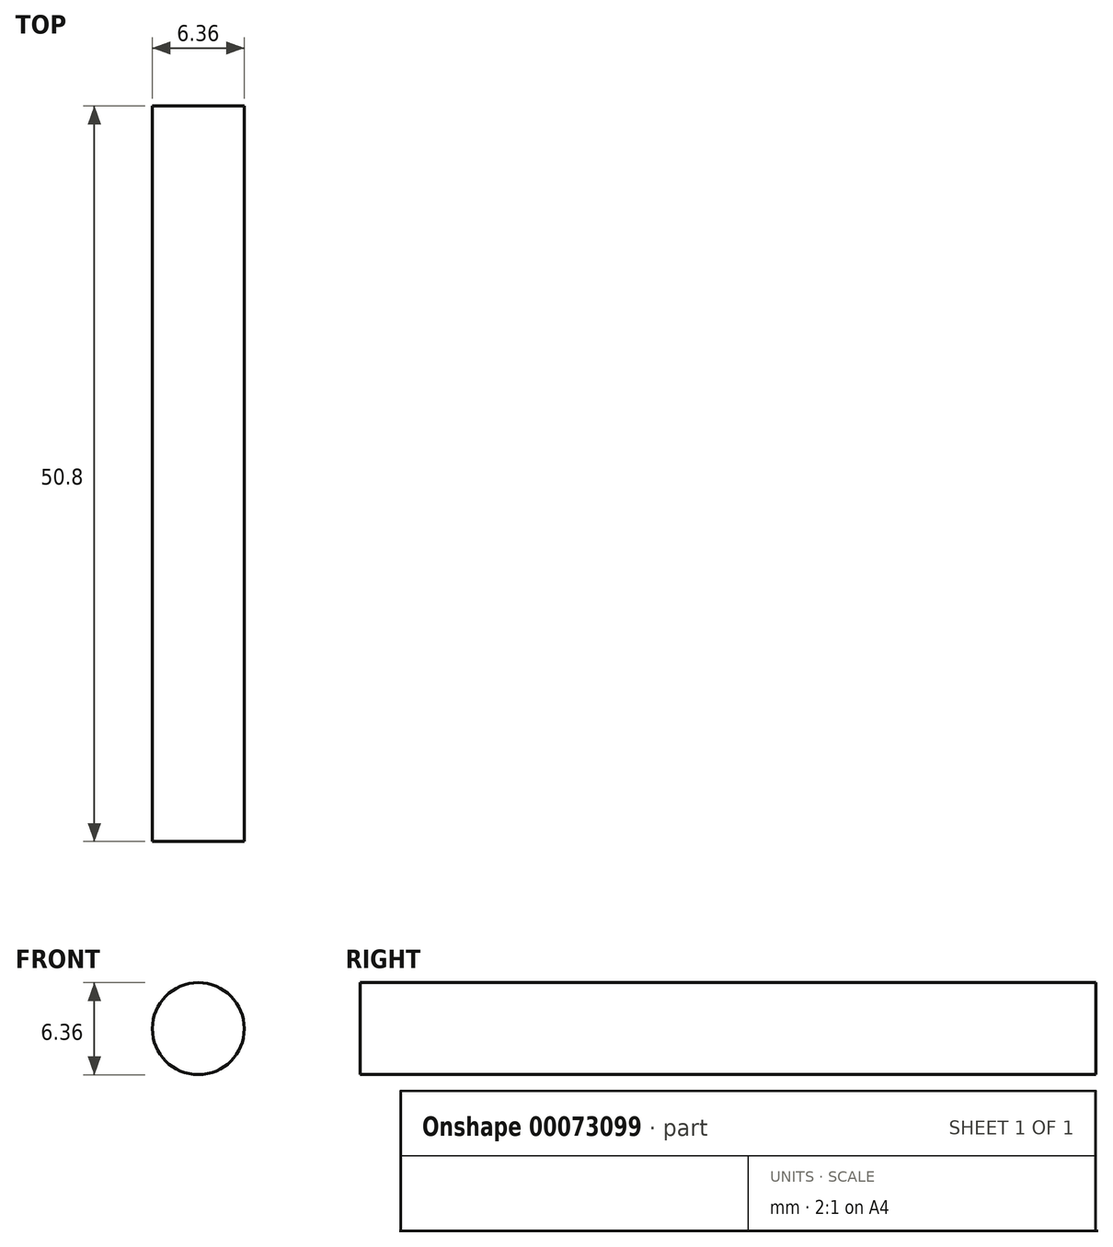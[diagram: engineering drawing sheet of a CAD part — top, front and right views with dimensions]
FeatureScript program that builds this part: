
annotation { "Feature Type Name" : "Feature", "Feature Type Description" : "" }
export const myFeature = defineFeature(function(context is Context, id is Id, definition is map)
    precondition{}
    {
        {
            var Q0;
            Q0=qCreatedBy(makeId("Front.planeOp"),FACE);
            var sketch = newSketch(context, id + "F0", { "sketchPlane" : qUnion([Q0])});
            skCircle(sketch, "E0", {"center": v(0, 0) * mm, "radius": 3.18 * mm});
            skSolve(sketch);
        }
        {
            var Q0;
            Q0=makeQuery(id+"F0.imprint","IMPRINT",FACE,{"disambiguationData":[TD([[makeQuery(id+"F0.imprint","IMPRINT",EDGE,{"derivedFrom":sQuery(id+"F0.wireOp",EDGE,"E0")}),1.0]])]});
            extrude(context, id + "F1", {"entities" : qUnion([Q0]), "endBound" : BoundingType.SYMMETRIC, "depth" : 50.8 * mm});
        }
    });
